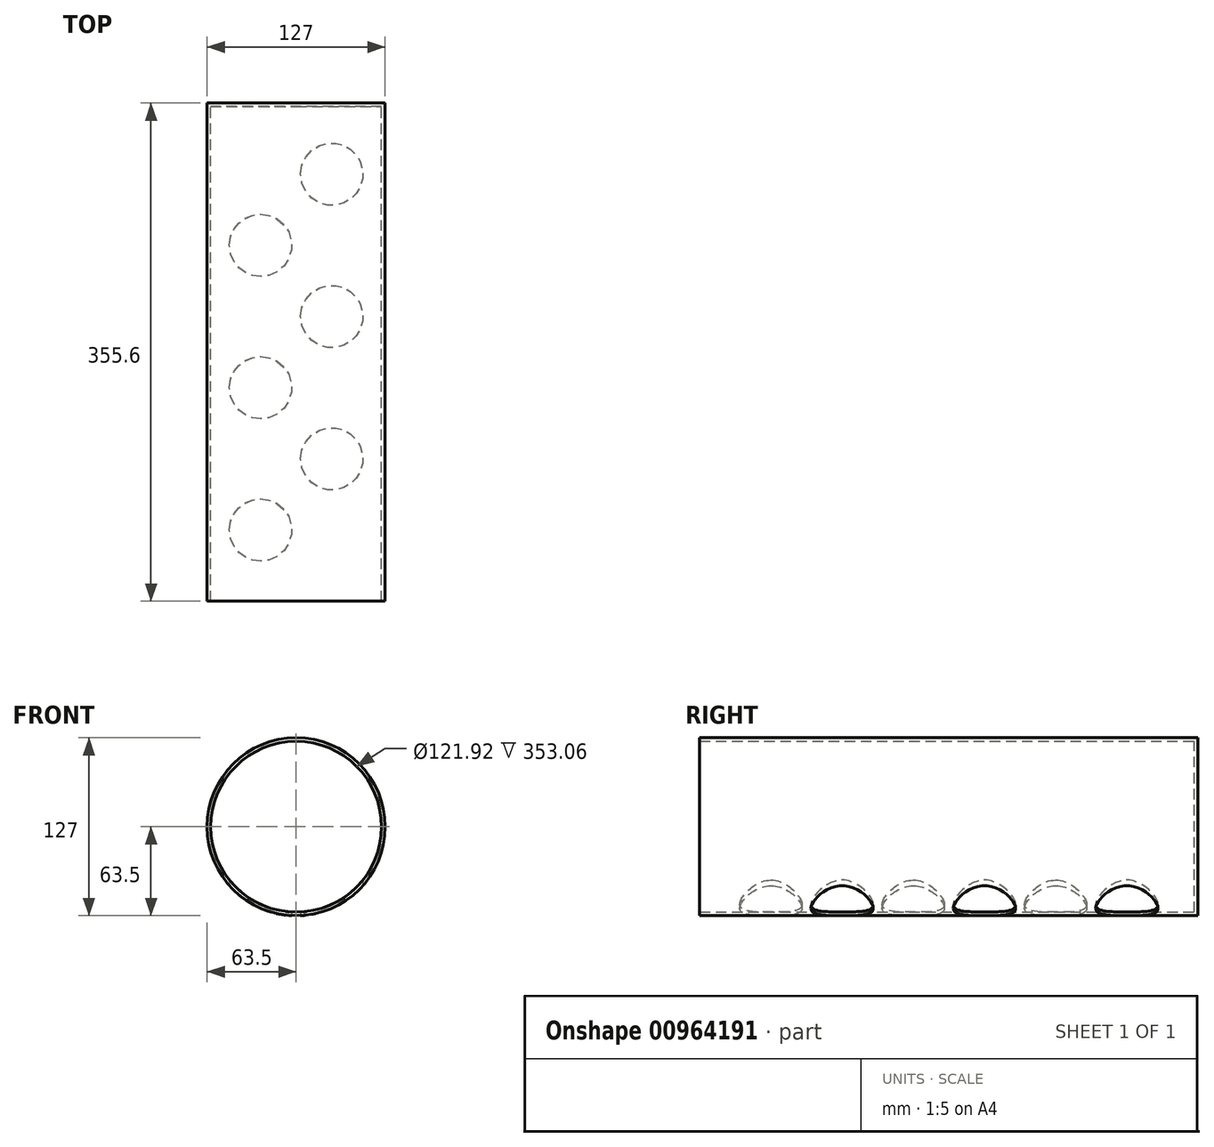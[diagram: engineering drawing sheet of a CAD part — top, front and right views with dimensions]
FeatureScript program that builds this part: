
annotation { "Feature Type Name" : "Feature", "Feature Type Description" : "" }
export const myFeature = defineFeature(function(context is Context, id is Id, definition is map)
    precondition{}
    {
        {
            var Q0;
            Q0=qCreatedBy(makeId("Front.planeOp"),FACE);
            var sketch = newSketch(context, id + "F0", { "sketchPlane" : qUnion([Q0])});
            skPoint(sketch, "E0", {"position": v(0, 63.5) * mm});
            skCircle(sketch, "E1", {"center": v(0, 63.5) * mm, "radius": 63.5 * mm});
            skSolve(sketch);
        }
        {
            var Q0;
            Q0 = qSketchRegion(id + "F0", true);
            extrude(context, id + "F1", {"entities" : qUnion([Q0]), "depth" : 355.6 * mm, "offsetDistance" : 25.4 * mm});
        }
        {
            var Q0;
            Q0 = qSketchRegion(id + "F0", true);
            extrude(context, id + "F2", {"entities" : qUnion([Q0]), "operationType" : NewBodyOperationType.ADD, "depth" : 355.6 * mm, "offsetDistance" : 25.4 * mm});
        }
        {
            var Q0;
            Q0=qCreatedBy(makeId("Top.planeOp"),FACE);
            var sketch = newSketch(context, id + "F3", { "sketchPlane" : qUnion([Q0])});
            skPoint(sketch, "E2", {"position": v(0, -153.12) * mm});
            skPoint(sketch, "E3", {"position": v(-25.4, 0) * mm});
            skPoint(sketch, "E4", {"position": v(25.4, 0) * mm});
            skPoint(sketch, "E5", {"position": v(-25.4, -101.6) * mm});
            skPoint(sketch, "E6", {"position": v(25.4, -50.8) * mm});
            skPoint(sketch, "E7", {"position": v(-25.4, -203.2) * mm});
            skPoint(sketch, "E8", {"position": v(-25.4, -304.8) * mm});
            skPoint(sketch, "E9", {"position": v(25.4, -152.4) * mm});
            skPoint(sketch, "E10", {"position": v(25.4, -254) * mm});
            skCircle(sketch, "E11", {"center": v(-25.4, -304.8) * mm, "radius": 22.23 * mm});
            skCircle(sketch, "E12", {"center": v(25.4, -254) * mm, "radius": 22.23 * mm});
            skCircle(sketch, "E13", {"center": v(-25.4, -203.2) * mm, "radius": 22.23 * mm});
            skCircle(sketch, "E14", {"center": v(25.4, -152.4) * mm, "radius": 22.23 * mm});
            skCircle(sketch, "E15", {"center": v(-25.4, -101.6) * mm, "radius": 22.23 * mm});
            skCircle(sketch, "E16", {"center": v(25.4, -50.8) * mm, "radius": 22.23 * mm});
            skSolve(sketch);
        }
        {
            var Q0;
            Q0=makeQuery(id+"F1.opExtrude","CAP_FACE",FACE,{"disambiguationData":[OSD([sQuery(id+"F0.wireOp",EDGE,"E1")])],"isStart":false});
            shell(context, id + "F4", {"entities" : qUnion([Q0]), "thickness" : 2.54 * mm});
        }
        {
            var Q0;
            Q0=sQuery(id+"F3.wireOp",VERTEX,"E8");
            var Q1;
            Q1=sQuery(id+"F3.wireOp",VERTEX,"E10");
            var Q2;
            Q2=sQuery(id+"F3.wireOp",VERTEX,"E7");
            var Q3;
            Q3=sQuery(id+"F3.wireOp",VERTEX,"E9");
            var Q4;
            Q4=sQuery(id+"F3.wireOp",VERTEX,"E5");
            var Q5;
            Q5=sQuery(id+"F3.wireOp",VERTEX,"E6");
            var Q6;
            Q6=makeQuery(id+"F1.opExtrude","SWEPT_BODY",BODY,{"disambiguationData":[OSD([sQuery(id+"F0.wireOp",EDGE,"E1")])]});
            hole(context, id + "F5", {"style" : HoleStyle.SIMPLE, "endStyle" : HoleEndStyle.BLIND, "oppositeDirection" : true, "holeDiameter" : 44.45 * mm, "majorDiameter" : 6.35 * mm, "holeDepth" : 12.7 * mm, "isTappedThrough" : true, "tappedDepth" : 12.7 * mm, "tapClearance" : 3, "locations" : qUnion([Q0, Q1, Q2, Q3, Q4, Q5]), "scope" : qUnion([Q6])});
        }
    });
